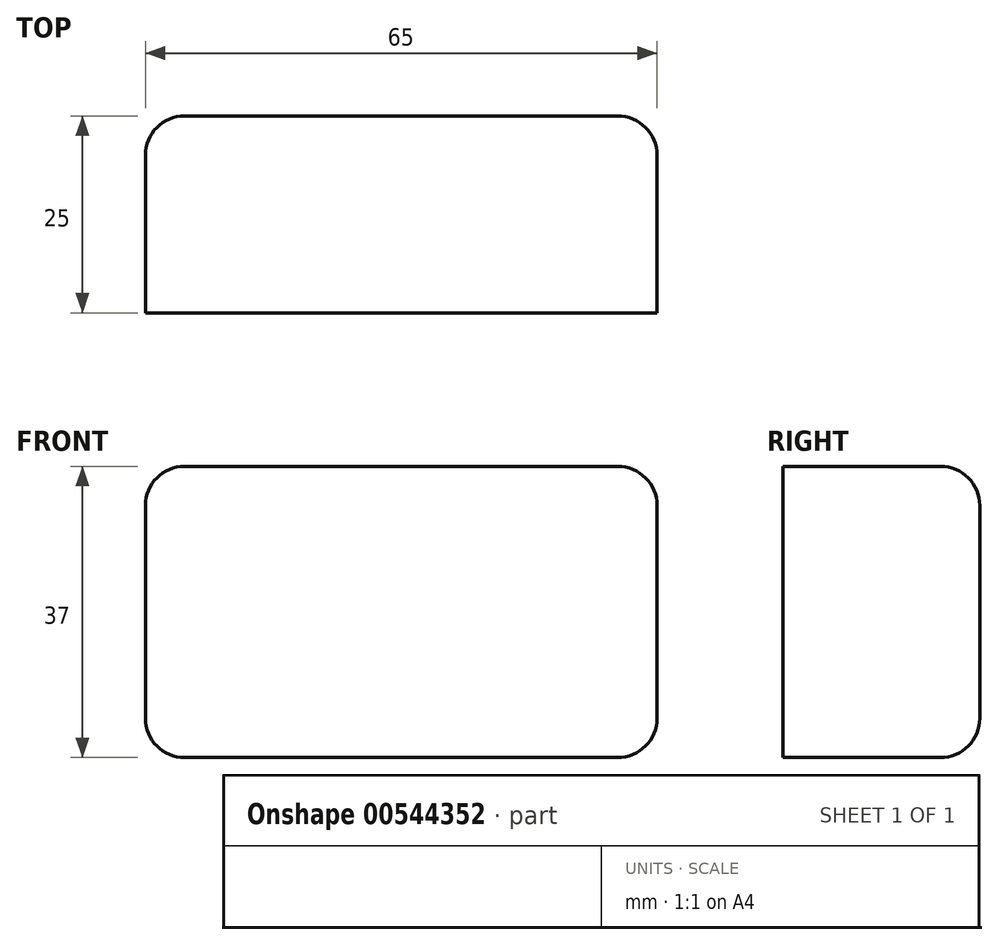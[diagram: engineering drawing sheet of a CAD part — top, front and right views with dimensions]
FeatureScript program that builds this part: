
annotation { "Feature Type Name" : "Feature", "Feature Type Description" : "" }
export const myFeature = defineFeature(function(context is Context, id is Id, definition is map)
    precondition{}
    {
        {
            var Q0;
            Q0=qCreatedBy(makeId("Front.planeOp"),FACE);
            var sketch = newSketch(context, id + "F0", { "sketchPlane" : qUnion([Q0])});
            skLineSegment(sketch, "E0.bottom", {"start": v(-32.5, 18.5) * mm, "end": v(32.5, 18.5) * mm});
            skLineSegment(sketch, "E0.top", {"start": v(-32.5, -18.5) * mm, "end": v(32.5, -18.5) * mm});
            skLineSegment(sketch, "E0.left", {"start": v(-32.5, 18.5) * mm, "end": v(-32.5, -18.5) * mm});
            skLineSegment(sketch, "E0.right", {"start": v(32.5, 18.5) * mm, "end": v(32.5, -18.5) * mm});
            skPoint(sketch, "E0.middle", {"position": v(0, 0) * mm});
            skSolve(sketch);
        }
        {
            var Q0;
            Q0 = qSketchRegion(id + "F0", true);
            extrude(context, id + "F1", {"entities" : qUnion([Q0]), "depth" : 25 * mm, "offsetDistance" : 25 * mm});
        }
        {
            var Q0;
            Q0=makeQuery(id+"F1.opExtrude","SWEPT_EDGE",EDGE,{"disambiguationData":[OSD([sQuery(id+"F0.wireOp",EDGE,"E0.bottom"),sQuery(id+"F0.wireOp",EDGE,"E0.left")])]});
            var Q1;
            Q1=makeQuery(id+"F1.opExtrude","SWEPT_EDGE",EDGE,{"disambiguationData":[OSD([sQuery(id+"F0.wireOp",EDGE,"E0.top"),sQuery(id+"F0.wireOp",EDGE,"E0.left")])]});
            var Q2;
            Q2=makeQuery(id+"F1.opExtrude","CAP_EDGE",EDGE,{"disambiguationData":[OSD([sQuery(id+"F0.wireOp",EDGE,"E0.bottom")])],"isStart":true});
            var Q3;
            Q3=makeQuery(id+"F1.opExtrude","CAP_EDGE",EDGE,{"disambiguationData":[OSD([sQuery(id+"F0.wireOp",EDGE,"E0.left")])],"isStart":true});
            var Q4;
            Q4=makeQuery(id+"F1.opExtrude","CAP_EDGE",EDGE,{"disambiguationData":[OSD([sQuery(id+"F0.wireOp",EDGE,"E0.right")])],"isStart":true});
            var Q5;
            Q5=makeQuery(id+"F1.opExtrude","SWEPT_EDGE",EDGE,{"disambiguationData":[OSD([sQuery(id+"F0.wireOp",EDGE,"E0.top"),sQuery(id+"F0.wireOp",EDGE,"E0.right")])]});
            var Q6;
            Q6=makeQuery(id+"F1.opExtrude","CAP_EDGE",EDGE,{"disambiguationData":[OSD([sQuery(id+"F0.wireOp",EDGE,"E0.top")])],"isStart":true});
            var Q7;
            Q7=makeQuery(id+"F1.opExtrude","CAP_FACE",FACE,{"disambiguationData":[OSD([sQuery(id+"F0.wireOp",EDGE,"E0.bottom"),sQuery(id+"F0.wireOp",EDGE,"E0.top"),sQuery(id+"F0.wireOp",EDGE,"E0.left"),sQuery(id+"F0.wireOp",EDGE,"E0.right")])],"isStart":true});
            fillet(context, id + "F2", {"entities" : qUnion([Q0, Q1, Q2, Q3, Q4, Q5, Q6, Q7]), "radius" : 5 * mm, "tangentPropagation" : true, "allowEdgeOverflow" : false});
        }
        {
            var Q0;
            Q0=makeQuery(id+"F2.opFillet","BLEND_EDGE",EDGE,{"blendedFrom":[makeQuery(id+"F1.opExtrude","CAP_EDGE",EDGE,{"disambiguationData":[OSD([sQuery(id+"F0.wireOp",EDGE,"E0.bottom")])],"isStart":true}),makeQuery(id+"F1.opExtrude","CAP_EDGE",EDGE,{"disambiguationData":[OSD([sQuery(id+"F0.wireOp",EDGE,"E0.right")])],"isStart":true})],"blendedInto":[]});
            fillet(context, id + "F3", {"entities" : qUnion([Q0]), "radius" : 5 * mm, "tangentPropagation" : true, "allowEdgeOverflow" : false});
        }
    });
